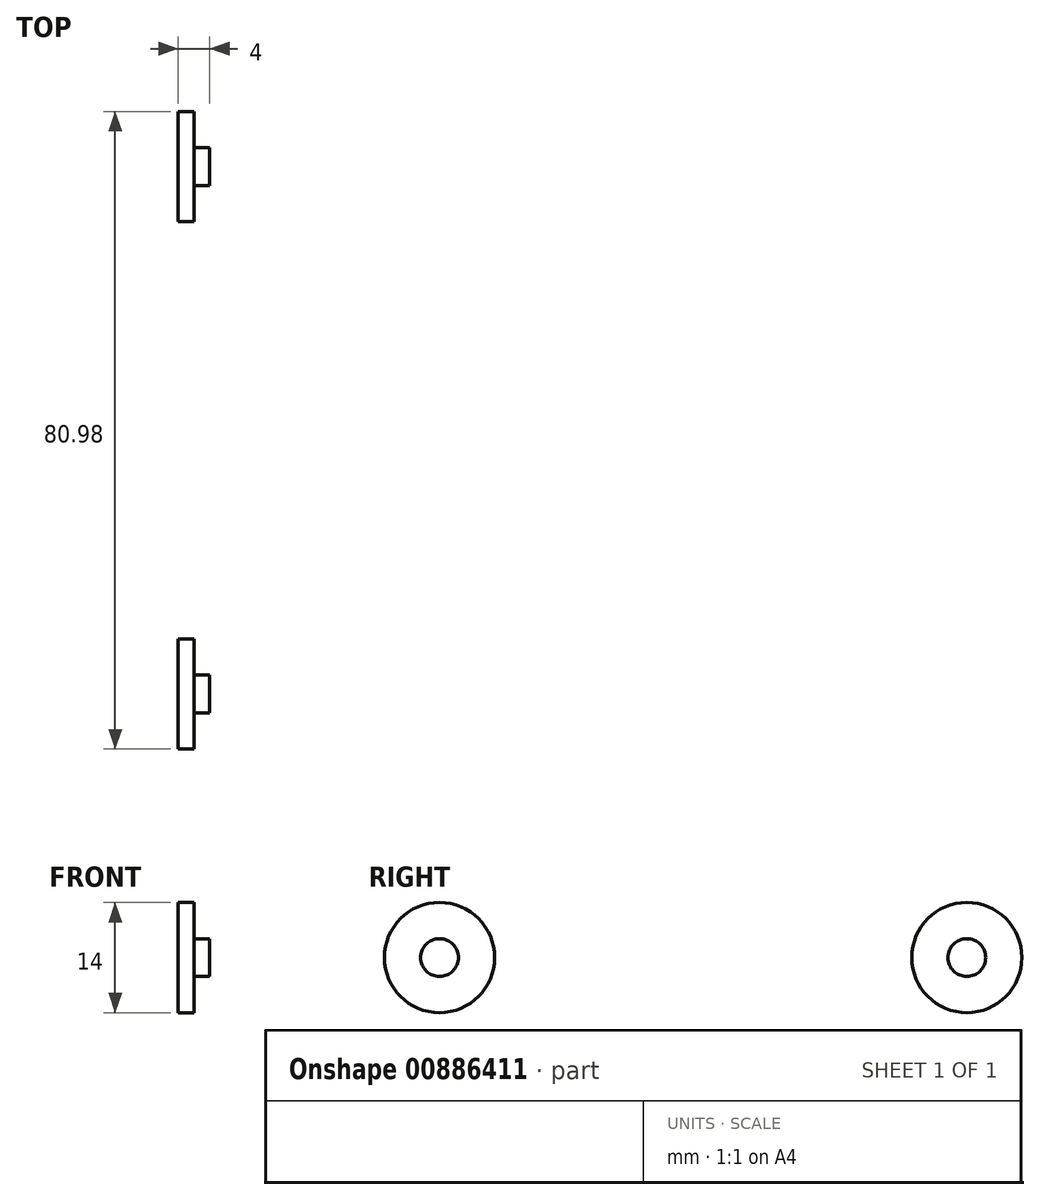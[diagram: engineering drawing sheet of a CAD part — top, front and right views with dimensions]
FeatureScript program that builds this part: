
annotation { "Feature Type Name" : "Feature", "Feature Type Description" : "" }
export const myFeature = defineFeature(function(context is Context, id is Id, definition is map)
    precondition{}
    {
        {
            var Q0;
            Q0=qCreatedBy(makeId("Right.planeOp"),FACE);
            var sketch = newSketch(context, id + "F0", { "sketchPlane" : qUnion([Q0])});
            skCircle(sketch, "E0", {"center": v(33.5, -42.87) * mm, "radius": 7 * mm});
            skSolve(sketch);
        }
        {
            var Q0;
            Q0 = qSketchRegion(id + "F0", true);
            extrude(context, id + "F1", {"entities" : qUnion([Q0]), "depth" : 2 * mm, "offsetDistance" : 25 * mm});
        }
        {
            var Q0;
            Q0=makeQuery(id+"F1.opExtrude","CAP_FACE",FACE,{"disambiguationData":[OSD([sQuery(id+"F0.wireOp",EDGE,"E0")])],"isStart":false});
            var sketch = newSketch(context, id + "F2", { "sketchPlane" : qUnion([Q0])});
            skCircle(sketch, "E1", {"center": v(33.5, -42.87) * mm, "radius": 2.4 * mm});
            skSolve(sketch);
        }
        {
            var Q0;
            Q0 = qSketchRegion(id + "F2", true);
            extrude(context, id + "F3", {"entities" : qUnion([Q0]), "operationType" : NewBodyOperationType.ADD, "depth" : 2 * mm, "offsetDistance" : 25 * mm});
        }
        {
            var Q0;
            Q0=makeQuery(id+"F1.opExtrude","SWEPT_BODY",BODY,{"disambiguationData":[OSD([sQuery(id+"F0.wireOp",EDGE,"E0")])]});
            var Q1;
            Q1=qCreatedBy(makeId("Front.planeOp"),FACE);
            mirror(context, id + "F4", {"entities" : qUnion([Q0]), "mirrorPlane" : qUnion([Q1])});
        }
    });
